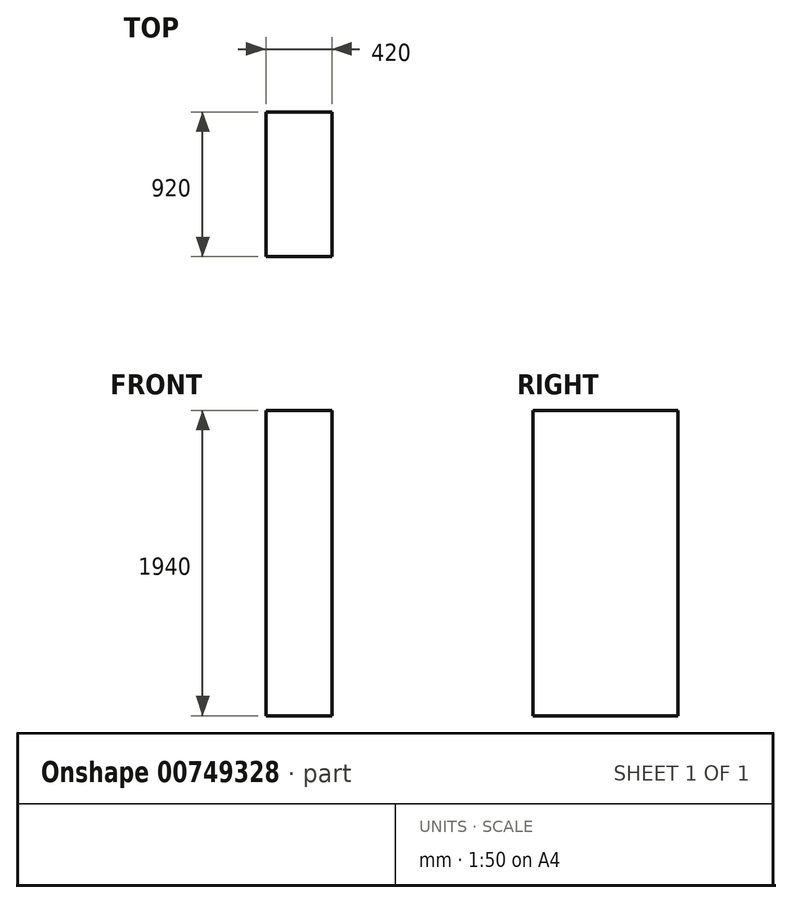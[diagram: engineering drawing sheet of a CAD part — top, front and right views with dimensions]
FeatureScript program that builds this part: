
annotation { "Feature Type Name" : "Feature", "Feature Type Description" : "" }
export const myFeature = defineFeature(function(context is Context, id is Id, definition is map)
    precondition{}
    {
        {
            var Q0;
            Q0=qCreatedBy(makeId("Top.planeOp"),FACE);
            var sketch = newSketch(context, id + "F0", { "sketchPlane" : qUnion([Q0])});
            skLineSegment(sketch, "E0.bottom", {"start": v(1141.28, 0) * mm, "end": v(1561.28, 0) * mm});
            skLineSegment(sketch, "E0.top", {"start": v(1141.28, 920) * mm, "end": v(1561.28, 920) * mm});
            skLineSegment(sketch, "E0.left", {"start": v(1141.28, 0) * mm, "end": v(1141.28, 920) * mm});
            skLineSegment(sketch, "E0.right", {"start": v(1561.28, 0) * mm, "end": v(1561.28, 920) * mm});
            skSolve(sketch);
        }
        {
            var Q0;
            Q0 = qSketchRegion(id + "F0", true);
            extrude(context, id + "F1", {"entities" : qUnion([Q0]), "depth" : 1940 * mm, "offsetDistance" : 25 * mm});
        }
    });
